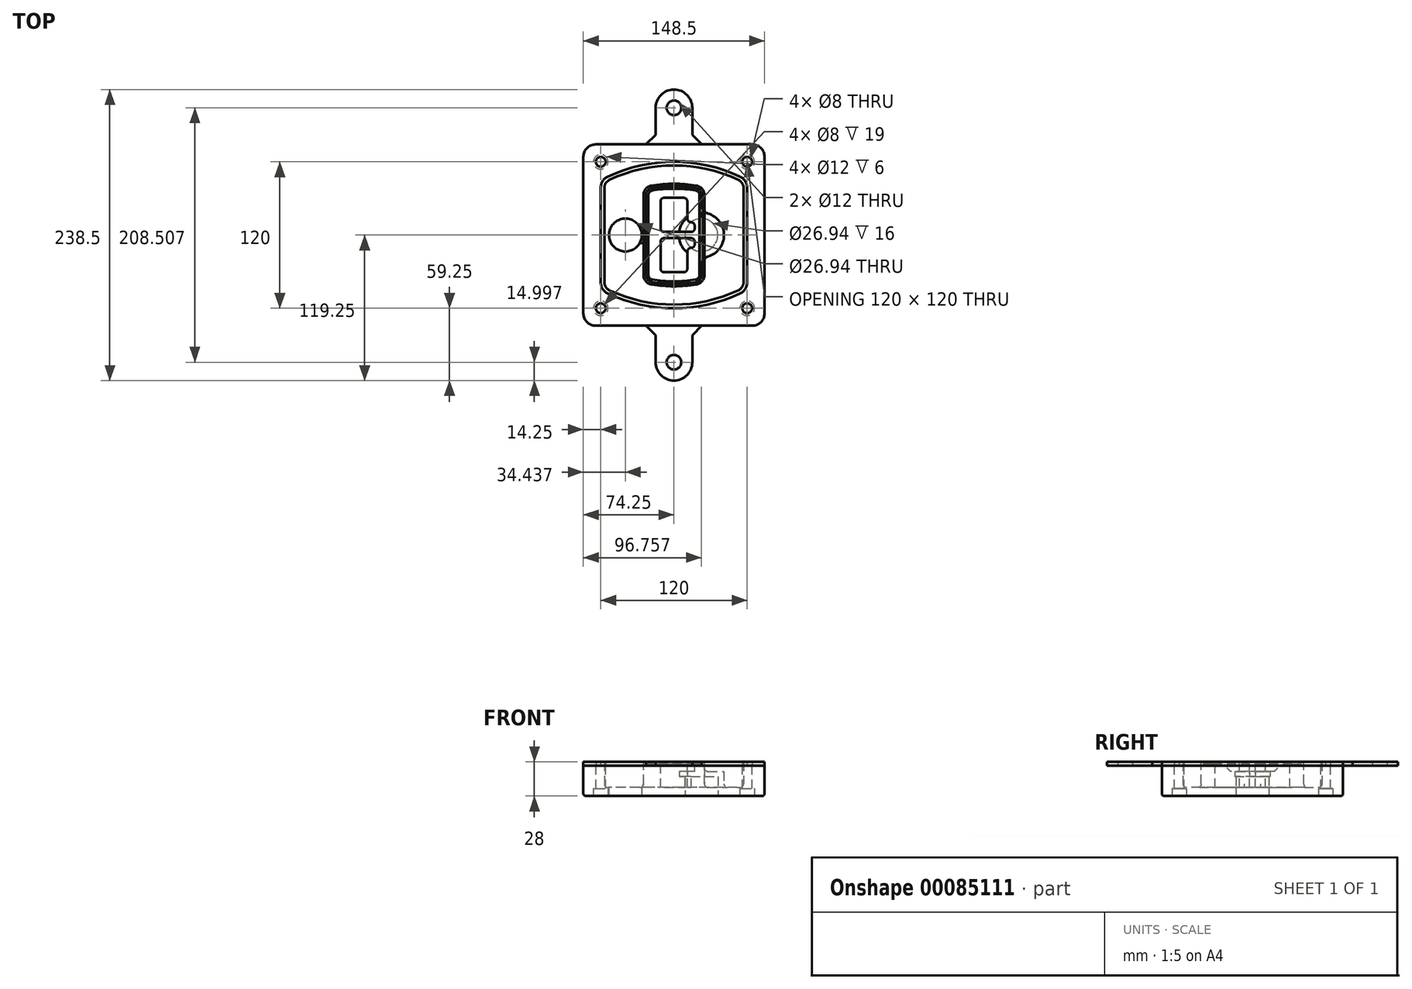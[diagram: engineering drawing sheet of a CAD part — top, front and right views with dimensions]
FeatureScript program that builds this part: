
annotation { "Feature Type Name" : "Feature", "Feature Type Description" : "" }
export const myFeature = defineFeature(function(context is Context, id is Id, definition is map)
    precondition{}
    {
        {
            var Q0;
            Q0=qCreatedBy(makeId("Top.planeOp"),FACE);
            var sketch = newSketch(context, id + "F0", { "sketchPlane" : qUnion([Q0])});
            skPoint(sketch, "E0.rect.middle", {"position": v(0, 0) * mm});
            skLineSegment(sketch, "E1.bottom", {"start": v(-64.25, -74.25) * mm, "end": v(64.25, -74.25) * mm});
            skLineSegment(sketch, "E1.top", {"start": v(-64.25, 74.25) * mm, "end": v(64.25, 74.25) * mm});
            skLineSegment(sketch, "E1.left", {"start": v(-74.25, -64.25) * mm, "end": v(-74.25, 64.25) * mm});
            skLineSegment(sketch, "E1.right", {"start": v(74.25, -64.25) * mm, "end": v(74.25, 64.25) * mm});
            skLineSegment(sketch, "E2", {"start": v(-74.25, 74.25) * mm, "end": v(74.25, -74.25) * mm, "construction": true});
            skLineSegment(sketch, "E3", {"start": v(74.25, 74.25) * mm, "end": v(-74.25, -74.25) * mm, "construction": true});
            skCircle(sketch, "E4", {"center": v(-60, 60) * mm, "radius": 4 * mm});
            skCircle(sketch, "E5", {"center": v(60, 60) * mm, "radius": 4 * mm});
            skCircle(sketch, "E6", {"center": v(60, -60) * mm, "radius": 4 * mm});
            skCircle(sketch, "E7", {"center": v(-60, -60) * mm, "radius": 4 * mm});
            skLineSegment(sketch, "E8", {"start": v(-60, 60) * mm, "end": v(60, 60) * mm, "construction": true});
            skLineSegment(sketch, "E9", {"start": v(60, 60) * mm, "end": v(60, -60) * mm, "construction": true});
            skLineSegment(sketch, "E10", {"start": v(60, -60) * mm, "end": v(-60, -60) * mm, "construction": true});
            skLineSegment(sketch, "E11", {"start": v(-60, -60) * mm, "end": v(-60, 60) * mm, "construction": true});
            skLineSegment(sketch, "E12", {"start": v(-60, 38.83) * mm, "end": v(-60, -38.83) * mm});
            skLineSegment(sketch, "E13", {"start": v(60, 38.83) * mm, "end": v(60, -38.83) * mm});
            skArc(sketch, "E14", {"start": v(54.26, 47.88) * mm, "mid": v(0, 60) * mm, "end": v(-54.26, 47.88) * mm});
            skArc(sketch, "E15", {"start": v(-54.26, -47.88) * mm, "mid": v(0, -60) * mm, "end": v(54.26, -47.88) * mm});
            skLineSegment(sketch, "E16", {"start": v(-60, 0) * mm, "end": v(60, 0) * mm, "construction": true});
            skPoint(sketch, "E17.visualSharp", {"position": v(-60, -45) * mm});
            skArc(sketch, "E17.filletArc", {"start": v(-60, -38.83) * mm, "mid": v(-58.44, -44.2) * mm, "end": v(-54.26, -47.88) * mm});
            skPoint(sketch, "E18.visualSharp", {"position": v(-60, 45) * mm});
            skArc(sketch, "E18.filletArc", {"start": v(-54.26, 47.88) * mm, "mid": v(-58.44, 44.2) * mm, "end": v(-60, 38.83) * mm});
            skPoint(sketch, "E19.visualSharp", {"position": v(60, 45) * mm});
            skArc(sketch, "E19.filletArc", {"start": v(60, 38.83) * mm, "mid": v(58.44, 44.2) * mm, "end": v(54.26, 47.88) * mm});
            skPoint(sketch, "E20.visualSharp", {"position": v(60, -45) * mm});
            skArc(sketch, "E20.filletArc", {"start": v(54.26, -47.88) * mm, "mid": v(58.44, -44.2) * mm, "end": v(60, -38.83) * mm});
            skPoint(sketch, "E21.visualSharp", {"position": v(-74.25, 74.25) * mm});
            skArc(sketch, "E21.filletArc", {"start": v(-64.25, 74.25) * mm, "mid": v(-71.32, 71.32) * mm, "end": v(-74.25, 64.25) * mm});
            skPoint(sketch, "E22.visualSharp", {"position": v(74.25, 74.25) * mm});
            skArc(sketch, "E22.filletArc", {"start": v(74.25, 64.25) * mm, "mid": v(71.32, 71.32) * mm, "end": v(64.25, 74.25) * mm});
            skPoint(sketch, "E23.visualSharp", {"position": v(74.25, -74.25) * mm});
            skArc(sketch, "E23.filletArc", {"start": v(64.25, -74.25) * mm, "mid": v(71.32, -71.32) * mm, "end": v(74.25, -64.25) * mm});
            skPoint(sketch, "E24.visualSharp", {"position": v(-74.25, -74.25) * mm});
            skArc(sketch, "E24.filletArc", {"start": v(-74.25, -64.25) * mm, "mid": v(-71.32, -71.32) * mm, "end": v(-64.25, -74.25) * mm});
            skArc(sketch, "E25.0", {"start": v(57, 38.83) * mm, "mid": v(55.9, 42.58) * mm, "end": v(52.98, 45.17) * mm});
            skLineSegment(sketch, "E25.1", {"start": v(57, 38.83) * mm, "end": v(57, -38.83) * mm});
            skArc(sketch, "E25.2", {"start": v(52.98, -45.17) * mm, "mid": v(55.9, -42.58) * mm, "end": v(57, -38.83) * mm});
            skArc(sketch, "E25.3", {"start": v(-52.98, -45.17) * mm, "mid": v(0, -57) * mm, "end": v(52.98, -45.17) * mm});
            skArc(sketch, "E25.4", {"start": v(-57, -38.83) * mm, "mid": v(-55.9, -42.58) * mm, "end": v(-52.98, -45.17) * mm});
            skArc(sketch, "E25.5", {"start": v(52.98, 45.17) * mm, "mid": v(0, 57) * mm, "end": v(-52.98, 45.17) * mm});
            skLineSegment(sketch, "E25.6", {"start": v(-57, 38.83) * mm, "end": v(-57, -38.83) * mm});
            skArc(sketch, "E25.7", {"start": v(-52.98, 45.17) * mm, "mid": v(-55.9, 42.58) * mm, "end": v(-57, 38.83) * mm});
            skArc(sketch, "E26.0", {"start": v(-55.96, 51.5) * mm, "mid": v(-61.82, 46.33) * mm, "end": v(-64, 38.83) * mm});
            skArc(sketch, "E26.1", {"start": v(55.96, 51.5) * mm, "mid": v(0, 64) * mm, "end": v(-55.96, 51.5) * mm});
            skArc(sketch, "E26.2", {"start": v(64, 38.83) * mm, "mid": v(61.82, 46.33) * mm, "end": v(55.96, 51.5) * mm});
            skLineSegment(sketch, "E26.3", {"start": v(64, 38.83) * mm, "end": v(64, -38.83) * mm});
            skArc(sketch, "E26.4", {"start": v(55.96, -51.5) * mm, "mid": v(61.82, -46.33) * mm, "end": v(64, -38.83) * mm});
            skLineSegment(sketch, "E26.5", {"start": v(-64, 38.83) * mm, "end": v(-64, -38.83) * mm});
            skArc(sketch, "E26.6", {"start": v(-55.96, -51.5) * mm, "mid": v(0, -64) * mm, "end": v(55.96, -51.5) * mm});
            skArc(sketch, "E26.7", {"start": v(-64, -38.83) * mm, "mid": v(-61.82, -46.33) * mm, "end": v(-55.96, -51.5) * mm});
            skSolve(sketch);
        }
        {
            var Q0;
            Q0=makeQuery(id+"F0.imprint","IMPRINT",FACE,{"disambiguationData":[TD([[makeQuery(id+"F0.imprint","IMPRINT",EDGE,{"derivedFrom":sQuery(id+"F0.wireOp",EDGE,"E1.bottom")}),1.0]])]});
            var Q1;
            Q1=makeQuery(id+"F0.imprint","IMPRINT",FACE,{"disambiguationData":[TD([[makeQuery(id+"F0.imprint","IMPRINT",EDGE,{"derivedFrom":sQuery(id+"F0.wireOp",EDGE,"E12")}),1.0]])]});
            var Q2;
            Q2=makeQuery(id+"F0.imprint","IMPRINT",FACE,{"disambiguationData":[TD([[makeQuery(id+"F0.imprint","IMPRINT",EDGE,{"derivedFrom":sQuery(id+"F0.wireOp",EDGE,"E25.0")}),1.0]])]});
            var Q3;
            Q3=makeQuery(id+"F0.imprint","IMPRINT",FACE,{"disambiguationData":[TD([[makeQuery(id+"F0.imprint","IMPRINT",EDGE,{"derivedFrom":sQuery(id+"F0.wireOp",EDGE,"E12")}),-1.0]])]});
            extrude(context, id + "F1", {"entities" : qUnion([Q0, Q1, Q2, Q3]), "oppositeDirection" : true, "depth" : 25 * mm});
        }
        {
            var Q0;
            Q0=makeQuery(id+"F0.imprint","IMPRINT",FACE,{"disambiguationData":[TD([[makeQuery(id+"F0.imprint","IMPRINT",EDGE,{"derivedFrom":sQuery(id+"F0.wireOp",EDGE,"E12")}),1.0]])]});
            extrude(context, id + "F2", {"entities" : qUnion([Q0]), "operationType" : NewBodyOperationType.ADD, "depth" : 3 * mm});
        }
        {
            var Q0;
            Q0=makeQuery(id+"F0.imprint","IMPRINT",FACE,{"disambiguationData":[TD([[makeQuery(id+"F0.imprint","IMPRINT",EDGE,{"derivedFrom":sQuery(id+"F0.wireOp",EDGE,"E25.0")}),1.0]])]});
            extrude(context, id + "F3", {"entities" : qUnion([Q0]), "operationType" : NewBodyOperationType.REMOVE, "oppositeDirection" : true, "depth" : 18 * mm});
        }
        {
            var Q0;
            Q0=makeQuery(id+"F2.opExtrude","CAP_FACE",FACE,{"disambiguationData":[OSD([sQuery(id+"F0.wireOp",EDGE,"E12"),sQuery(id+"F0.wireOp",EDGE,"E13"),sQuery(id+"F0.wireOp",EDGE,"E14"),sQuery(id+"F0.wireOp",EDGE,"E15"),sQuery(id+"F0.wireOp",EDGE,"E17.filletArc"),sQuery(id+"F0.wireOp",EDGE,"E18.filletArc"),sQuery(id+"F0.wireOp",EDGE,"E19.filletArc"),sQuery(id+"F0.wireOp",EDGE,"E20.filletArc"),sQuery(id+"F0.wireOp",EDGE,"E25.0"),sQuery(id+"F0.wireOp",EDGE,"E25.1"),sQuery(id+"F0.wireOp",EDGE,"E25.2"),sQuery(id+"F0.wireOp",EDGE,"E25.3"),sQuery(id+"F0.wireOp",EDGE,"E25.4"),sQuery(id+"F0.wireOp",EDGE,"E25.5"),sQuery(id+"F0.wireOp",EDGE,"E25.6"),sQuery(id+"F0.wireOp",EDGE,"E25.7")])],"isStart":false});
            var sketch = newSketch(context, id + "F4", { "sketchPlane" : qUnion([Q0])});
            skArc(sketch, "E27.0", {"start": v(-18.34, -40.45) * mm, "mid": v(0, -42) * mm, "end": v(18.34, -40.45) * mm});
            skArc(sketch, "E28.0", {"start": v(18.34, 40.45) * mm, "mid": v(0, 42) * mm, "end": v(-18.34, 40.45) * mm});
            skLineSegment(sketch, "E29", {"start": v(-25, 32.57) * mm, "end": v(-25, -32.57) * mm});
            skLineSegment(sketch, "E30", {"start": v(25, 32.57) * mm, "end": v(25, -32.57) * mm});
            skLineSegment(sketch, "E31", {"start": v(-25, 39.1) * mm, "end": v(25, 39.1) * mm, "construction": true});
            skLineSegment(sketch, "E32", {"start": v(-25, -39.1) * mm, "end": v(25, -39.1) * mm, "construction": true});
            skPoint(sketch, "E33.visualSharp", {"position": v(-25, 39.1) * mm});
            skArc(sketch, "E33.filletArc", {"start": v(-18.34, 40.45) * mm, "mid": v(-23.11, 37.73) * mm, "end": v(-25, 32.57) * mm});
            skPoint(sketch, "E34.visualSharp", {"position": v(25, 39.1) * mm});
            skArc(sketch, "E34.filletArc", {"start": v(25, 32.57) * mm, "mid": v(23.11, 37.73) * mm, "end": v(18.34, 40.45) * mm});
            skPoint(sketch, "E35.visualSharp", {"position": v(25, -39.1) * mm});
            skArc(sketch, "E35.filletArc", {"start": v(18.34, -40.45) * mm, "mid": v(23.11, -37.73) * mm, "end": v(25, -32.57) * mm});
            skPoint(sketch, "E36.visualSharp", {"position": v(-25, -39.1) * mm});
            skArc(sketch, "E36.filletArc", {"start": v(-25, -32.57) * mm, "mid": v(-23.11, -37.73) * mm, "end": v(-18.34, -40.45) * mm});
            skArc(sketch, "E37.0", {"start": v(52.98, 45.17) * mm, "mid": v(0, 57) * mm, "end": v(-52.98, 45.17) * mm});
            skArc(sketch, "E37.1", {"start": v(-52.98, 45.17) * mm, "mid": v(-55.9, 42.58) * mm, "end": v(-57, 38.83) * mm});
            skLineSegment(sketch, "E37.2", {"start": v(-57, 38.83) * mm, "end": v(-57, -38.83) * mm});
            skArc(sketch, "E37.3", {"start": v(-57, -38.83) * mm, "mid": v(-55.9, -42.58) * mm, "end": v(-52.98, -45.17) * mm});
            skArc(sketch, "E37.4", {"start": v(-52.98, -45.17) * mm, "mid": v(0, -57) * mm, "end": v(52.98, -45.17) * mm});
            skArc(sketch, "E37.5", {"start": v(52.98, -45.17) * mm, "mid": v(55.9, -42.58) * mm, "end": v(57, -38.83) * mm});
            skLineSegment(sketch, "E37.6", {"start": v(57, 38.83) * mm, "end": v(57, -38.83) * mm});
            skArc(sketch, "E37.7", {"start": v(57, 38.83) * mm, "mid": v(55.9, 42.58) * mm, "end": v(52.98, 45.17) * mm});
            skLineSegment(sketch, "E38.0", {"start": v(23, 32.57) * mm, "end": v(23, -32.57) * mm});
            skArc(sketch, "E38.1", {"start": v(18, -38.48) * mm, "mid": v(21.58, -36.44) * mm, "end": v(23, -32.57) * mm});
            skArc(sketch, "E38.2", {"start": v(-18, -38.48) * mm, "mid": v(0, -40) * mm, "end": v(18, -38.48) * mm});
            skArc(sketch, "E38.3", {"start": v(-23, -32.57) * mm, "mid": v(-21.58, -36.44) * mm, "end": v(-18, -38.48) * mm});
            skLineSegment(sketch, "E38.4", {"start": v(-23, 32.57) * mm, "end": v(-23, -32.57) * mm});
            skArc(sketch, "E38.5", {"start": v(23, 32.57) * mm, "mid": v(21.58, 36.44) * mm, "end": v(18, 38.48) * mm});
            skArc(sketch, "E38.6", {"start": v(-18, 38.48) * mm, "mid": v(-21.58, 36.44) * mm, "end": v(-23, 32.57) * mm});
            skArc(sketch, "E38.7", {"start": v(18, 38.48) * mm, "mid": v(0, 40) * mm, "end": v(-18, 38.48) * mm});
            skArc(sketch, "E39.0", {"start": v(21, 32.57) * mm, "mid": v(20.06, 35.15) * mm, "end": v(17.67, 36.5) * mm});
            skLineSegment(sketch, "E39.1", {"start": v(21, 32.57) * mm, "end": v(21, -32.57) * mm});
            skArc(sketch, "E39.2", {"start": v(17.67, -36.5) * mm, "mid": v(20.06, -35.15) * mm, "end": v(21, -32.57) * mm});
            skArc(sketch, "E39.3", {"start": v(-17.67, -36.5) * mm, "mid": v(0, -38) * mm, "end": v(17.67, -36.5) * mm});
            skArc(sketch, "E39.4", {"start": v(-21, -32.57) * mm, "mid": v(-20.06, -35.15) * mm, "end": v(-17.67, -36.5) * mm});
            skArc(sketch, "E39.5", {"start": v(17.67, 36.5) * mm, "mid": v(0, 38) * mm, "end": v(-17.67, 36.5) * mm});
            skLineSegment(sketch, "E39.6", {"start": v(-21, 32.57) * mm, "end": v(-21, -32.57) * mm});
            skArc(sketch, "E39.7", {"start": v(-17.67, 36.5) * mm, "mid": v(-20.06, 35.15) * mm, "end": v(-21, 32.57) * mm});
            skLineSegment(sketch, "E40", {"start": v(-25, 0) * mm, "end": v(25, 0) * mm, "construction": true});
            skLineSegment(sketch, "E41", {"start": v(-11, 5.5) * mm, "end": v(-11, 27.5) * mm});
            skLineSegment(sketch, "E42", {"start": v(-8, 30.5) * mm, "end": v(8, 30.5) * mm});
            skLineSegment(sketch, "E43", {"start": v(11, 27.5) * mm, "end": v(11, 13.5) * mm});
            skLineSegment(sketch, "E44", {"start": v(14, 10.5) * mm, "end": v(14, 10.5) * mm});
            skLineSegment(sketch, "E45", {"start": v(17, 7.5) * mm, "end": v(17, 5.5) * mm});
            skLineSegment(sketch, "E46", {"start": v(14, 2.5) * mm, "end": v(-8, 2.5) * mm});
            skPoint(sketch, "E47.visualSharp", {"position": v(-11, 30.5) * mm});
            skArc(sketch, "E47.filletArc", {"start": v(-8, 30.5) * mm, "mid": v(-10.12, 29.62) * mm, "end": v(-11, 27.5) * mm});
            skPoint(sketch, "E48.visualSharp", {"position": v(11, 30.5) * mm});
            skArc(sketch, "E48.filletArc", {"start": v(11, 27.5) * mm, "mid": v(10.12, 29.62) * mm, "end": v(8, 30.5) * mm});
            skPoint(sketch, "E49.visualSharp", {"position": v(11, 10.5) * mm});
            skArc(sketch, "E49.filletArc", {"start": v(11, 13.5) * mm, "mid": v(11.88, 11.38) * mm, "end": v(14, 10.5) * mm});
            skPoint(sketch, "E50.visualSharp", {"position": v(17, 10.5) * mm});
            skArc(sketch, "E50.filletArc", {"start": v(17, 7.5) * mm, "mid": v(16.12, 9.62) * mm, "end": v(14, 10.5) * mm});
            skPoint(sketch, "E51.visualSharp", {"position": v(17, 2.5) * mm});
            skArc(sketch, "E51.filletArc", {"start": v(14, 2.5) * mm, "mid": v(16.12, 3.38) * mm, "end": v(17, 5.5) * mm});
            skPoint(sketch, "E52.visualSharp", {"position": v(-11, 2.5) * mm});
            skArc(sketch, "E52.filletArc", {"start": v(-11, 5.5) * mm, "mid": v(-10.12, 3.38) * mm, "end": v(-8, 2.5) * mm});
            skLineSegment(sketch, "E53.0.MirrorCS", {"start": v(14, -2.5) * mm, "end": v(-8, -2.5) * mm});
            skArc(sketch, "E54.0.MirrorCS", {"start": v(-11, -5.5) * mm, "mid": v(-10.12, -3.38) * mm, "end": v(-8, -2.5) * mm});
            skLineSegment(sketch, "E55.0.MirrorCS", {"start": v(-11, -5.5) * mm, "end": v(-11, -27.5) * mm});
            skArc(sketch, "E56.0.MirrorCS", {"start": v(-8, -30.5) * mm, "mid": v(-10.12, -29.62) * mm, "end": v(-11, -27.5) * mm});
            skLineSegment(sketch, "E57.0.MirrorCS", {"start": v(-8, -30.5) * mm, "end": v(8, -30.5) * mm});
            skArc(sketch, "E58.0.MirrorCS", {"start": v(11, -27.5) * mm, "mid": v(10.12, -29.62) * mm, "end": v(8, -30.5) * mm});
            skLineSegment(sketch, "E59.0.MirrorCS", {"start": v(11, -27.5) * mm, "end": v(11, -13.5) * mm});
            skArc(sketch, "E60.0.MirrorCS", {"start": v(11, -13.5) * mm, "mid": v(11.88, -11.38) * mm, "end": v(14, -10.5) * mm});
            skArc(sketch, "E61.0.MirrorCS", {"start": v(17, -7.5) * mm, "mid": v(16.12, -9.62) * mm, "end": v(14, -10.5) * mm});
            skLineSegment(sketch, "E62.0.MirrorCS", {"start": v(17, -7.5) * mm, "end": v(17, -5.5) * mm});
            skArc(sketch, "E63.0.MirrorCS", {"start": v(14, -2.5) * mm, "mid": v(16.12, -3.38) * mm, "end": v(17, -5.5) * mm});
            skSolve(sketch);
        }
        {
            var Q0;
            Q0=makeQuery(id+"F4.imprint","IMPRINT",FACE,{"disambiguationData":[TD([[makeQuery(id+"F4.imprint","IMPRINT",EDGE,{"derivedFrom":sQuery(id+"F4.wireOp",EDGE,"E27.0")}),1.0]])]});
            var Q1;
            Q1=makeQuery(id+"F4.imprint","IMPRINT",FACE,{"disambiguationData":[TD([[makeQuery(id+"F4.imprint","IMPRINT",EDGE,{"derivedFrom":sQuery(id+"F4.wireOp",EDGE,"E38.0")}),-1.0]])]});
            var Q2;
            Q2=makeQuery(id+"F4.imprint","IMPRINT",FACE,{"disambiguationData":[TD([[makeQuery(id+"F4.imprint","IMPRINT",EDGE,{"derivedFrom":sQuery(id+"F4.wireOp",EDGE,"E39.0")}),1.0]])]});
            extrude(context, id + "F5", {"entities" : qUnion([Q0, Q1, Q2]), "operationType" : NewBodyOperationType.ADD, "endBound" : BoundingType.UP_TO_NEXT, "oppositeDirection" : true, "depth" : 25 * mm});
        }
        {
            var Q0;
            Q0=makeQuery(id+"F4.imprint","IMPRINT",FACE,{"disambiguationData":[TD([[makeQuery(id+"F4.imprint","IMPRINT",EDGE,{"derivedFrom":sQuery(id+"F4.wireOp",EDGE,"E38.0")}),-1.0]])]});
            extrude(context, id + "F6", {"entities" : qUnion([Q0]), "operationType" : NewBodyOperationType.REMOVE, "oppositeDirection" : true, "depth" : 2 * mm});
        }
        {
            var Q0;
            Q0=makeQuery(id+"F1.opExtrude","CAP_FACE",FACE,{"disambiguationData":[OSD([sQuery(id+"F0.wireOp",EDGE,"E1.bottom"),sQuery(id+"F0.wireOp",EDGE,"E1.top"),sQuery(id+"F0.wireOp",EDGE,"E1.left"),sQuery(id+"F0.wireOp",EDGE,"E1.right"),sQuery(id+"F0.wireOp",EDGE,"E4"),sQuery(id+"F0.wireOp",EDGE,"E5"),sQuery(id+"F0.wireOp",EDGE,"E6"),sQuery(id+"F0.wireOp",EDGE,"E7"),sQuery(id+"F0.wireOp",EDGE,"E21.filletArc"),sQuery(id+"F0.wireOp",EDGE,"E22.filletArc"),sQuery(id+"F0.wireOp",EDGE,"E23.filletArc"),sQuery(id+"F0.wireOp",EDGE,"E24.filletArc")])],"isStart":false});
            var sketch = newSketch(context, id + "F7", { "sketchPlane" : qUnion([Q0])});
            skCircle(sketch, "E64", {"center": v(22.5, 0) * mm, "radius": 13.47 * mm});
            skCircle(sketch, "E65", {"center": v(-39.81, 0) * mm, "radius": 13.47 * mm});
            skLineSegment(sketch, "E66", {"start": v(74.25, 0) * mm, "end": v(-74.25, 0) * mm});
            skCircle(sketch, "E67", {"center": v(22.5, 0) * mm, "radius": 18.47 * mm});
            skCircle(sketch, "E68", {"center": v(60, -60) * mm, "radius": 6 * mm});
            skCircle(sketch, "E69", {"center": v(-60, -60) * mm, "radius": 6 * mm});
            skCircle(sketch, "E70", {"center": v(-60, 60) * mm, "radius": 6 * mm});
            skCircle(sketch, "E71", {"center": v(60, 60) * mm, "radius": 6 * mm});
            skSolve(sketch);
        }
        {
            var Q0;
            {var subQ1=sQuery(id+"F7.wireOp",EDGE,"E66");var subQ4=sQuery(id+"F7.wireOp",EDGE,"E64");var subQ6=makeQuery(id+"F7.imprint","INTERSECT",VERTEX,{"disambiguationData":[OD(0.0)],"derivedFrom":[subQ4,subQ1]});Q0=makeQuery(id+"F7.imprint","IMPRINT",FACE,{"disambiguationData":[TD([[makeQuery(id+"F7.imprint","IMPRINT",EDGE,{"disambiguationData":[TD([[subQ6,-1.0]])],"derivedFrom":subQ4}),-1.0]])]});}
            var Q1;
            {var subQ0=sQuery(id+"F7.wireOp",EDGE,"E66");var subQ1=sQuery(id+"F7.wireOp",EDGE,"E64");var subQ3=makeQuery(id+"F7.imprint","INTERSECT",VERTEX,{"disambiguationData":[OD(0.0)],"derivedFrom":[subQ1,subQ0]});Q1=makeQuery(id+"F7.imprint","IMPRINT",FACE,{"disambiguationData":[TD([[makeQuery(id+"F7.imprint","IMPRINT",EDGE,{"disambiguationData":[TD([[subQ3,-1.0]])],"derivedFrom":subQ1}),1.0]])]});}
            var Q2;
            {var subQ0=sQuery(id+"F7.wireOp",EDGE,"E66");var subQ1=sQuery(id+"F7.wireOp",EDGE,"E64");var subQ3=makeQuery(id+"F7.imprint","INTERSECT",VERTEX,{"disambiguationData":[OD(0.0)],"derivedFrom":[subQ1,subQ0]});Q2=makeQuery(id+"F7.imprint","IMPRINT",FACE,{"disambiguationData":[TD([[makeQuery(id+"F7.imprint","IMPRINT",EDGE,{"disambiguationData":[TD([[subQ3,1.0]])],"derivedFrom":subQ1}),1.0]])]});}
            var Q3;
            {var subQ1=sQuery(id+"F7.wireOp",EDGE,"E66");var subQ4=sQuery(id+"F7.wireOp",EDGE,"E64");var subQ6=makeQuery(id+"F7.imprint","INTERSECT",VERTEX,{"disambiguationData":[OD(0.0)],"derivedFrom":[subQ4,subQ1]});Q3=makeQuery(id+"F7.imprint","IMPRINT",FACE,{"disambiguationData":[TD([[makeQuery(id+"F7.imprint","IMPRINT",EDGE,{"disambiguationData":[TD([[subQ6,1.0]])],"derivedFrom":subQ4}),-1.0]])]});}
            extrude(context, id + "F8", {"entities" : qUnion([Q0, Q1, Q2, Q3]), "operationType" : NewBodyOperationType.ADD, "oppositeDirection" : true, "depth" : 20 * mm});
        }
        {
            var Q0;
            {var subQ0=sQuery(id+"F7.wireOp",EDGE,"E66");var subQ1=sQuery(id+"F7.wireOp",EDGE,"E64");var subQ3=makeQuery(id+"F7.imprint","INTERSECT",VERTEX,{"disambiguationData":[OD(0.0)],"derivedFrom":[subQ1,subQ0]});Q0=makeQuery(id+"F7.imprint","IMPRINT",FACE,{"disambiguationData":[TD([[makeQuery(id+"F7.imprint","IMPRINT",EDGE,{"disambiguationData":[TD([[subQ3,-1.0]])],"derivedFrom":subQ1}),1.0]])]});}
            var Q1;
            {var subQ0=sQuery(id+"F7.wireOp",EDGE,"E66");var subQ1=sQuery(id+"F7.wireOp",EDGE,"E64");var subQ3=makeQuery(id+"F7.imprint","INTERSECT",VERTEX,{"disambiguationData":[OD(0.0)],"derivedFrom":[subQ1,subQ0]});Q1=makeQuery(id+"F7.imprint","IMPRINT",FACE,{"disambiguationData":[TD([[makeQuery(id+"F7.imprint","IMPRINT",EDGE,{"disambiguationData":[TD([[subQ3,1.0]])],"derivedFrom":subQ1}),1.0]])]});}
            extrude(context, id + "F9", {"entities" : qUnion([Q0, Q1]), "operationType" : NewBodyOperationType.REMOVE, "oppositeDirection" : true, "depth" : 16 * mm});
        }
        {
            var Q0;
            {var subQ0=sQuery(id+"F7.wireOp",EDGE,"E66");var subQ1=sQuery(id+"F7.wireOp",EDGE,"E65");var subQ3=makeQuery(id+"F7.imprint","INTERSECT",VERTEX,{"disambiguationData":[OD(0.0)],"derivedFrom":[subQ1,subQ0]});Q0=makeQuery(id+"F7.imprint","IMPRINT",FACE,{"disambiguationData":[TD([[makeQuery(id+"F7.imprint","IMPRINT",EDGE,{"disambiguationData":[TD([[subQ3,-1.0]])],"derivedFrom":subQ1}),1.0]])]});}
            var Q1;
            {var subQ0=sQuery(id+"F7.wireOp",EDGE,"E66");var subQ1=sQuery(id+"F7.wireOp",EDGE,"E65");var subQ3=makeQuery(id+"F7.imprint","INTERSECT",VERTEX,{"disambiguationData":[OD(0.0)],"derivedFrom":[subQ1,subQ0]});Q1=makeQuery(id+"F7.imprint","IMPRINT",FACE,{"disambiguationData":[TD([[makeQuery(id+"F7.imprint","IMPRINT",EDGE,{"disambiguationData":[TD([[subQ3,1.0]])],"derivedFrom":subQ1}),1.0]])]});}
            extrude(context, id + "F10", {"entities" : qUnion([Q0, Q1]), "operationType" : NewBodyOperationType.REMOVE, "oppositeDirection" : true, "depth" : 25 * mm});
        }
        {
            var Q0;
            Q0=makeQuery(id+"F7.imprint","IMPRINT",FACE,{"disambiguationData":[TD([[makeQuery(id+"F7.imprint","IMPRINT",EDGE,{"derivedFrom":sQuery(id+"F7.wireOp",EDGE,"E68")}),1.0]])]});
            var Q1;
            Q1=makeQuery(id+"F7.imprint","IMPRINT",FACE,{"disambiguationData":[TD([[makeQuery(id+"F7.imprint","IMPRINT",EDGE,{"derivedFrom":makeQuery(id+"F1.opExtrude","CAP_EDGE",EDGE,{"disambiguationData":[OSD([sQuery(id+"F0.wireOp",EDGE,"E5")])],"isStart":false})}),-1.0]])]});
            var Q2;
            Q2=makeQuery(id+"F7.imprint","IMPRINT",FACE,{"disambiguationData":[TD([[makeQuery(id+"F7.imprint","IMPRINT",EDGE,{"derivedFrom":sQuery(id+"F7.wireOp",EDGE,"E69")}),1.0]])]});
            var Q3;
            Q3=makeQuery(id+"F7.imprint","IMPRINT",FACE,{"disambiguationData":[TD([[makeQuery(id+"F7.imprint","IMPRINT",EDGE,{"derivedFrom":makeQuery(id+"F1.opExtrude","CAP_EDGE",EDGE,{"disambiguationData":[OSD([sQuery(id+"F0.wireOp",EDGE,"E4")])],"isStart":false})}),-1.0]])]});
            var Q4;
            Q4=makeQuery(id+"F7.imprint","IMPRINT",FACE,{"disambiguationData":[TD([[makeQuery(id+"F7.imprint","IMPRINT",EDGE,{"derivedFrom":sQuery(id+"F7.wireOp",EDGE,"E70")}),1.0]])]});
            var Q5;
            Q5=makeQuery(id+"F7.imprint","IMPRINT",FACE,{"disambiguationData":[TD([[makeQuery(id+"F7.imprint","IMPRINT",EDGE,{"derivedFrom":makeQuery(id+"F1.opExtrude","CAP_EDGE",EDGE,{"disambiguationData":[OSD([sQuery(id+"F0.wireOp",EDGE,"E7")])],"isStart":false})}),-1.0]])]});
            var Q6;
            Q6=makeQuery(id+"F7.imprint","IMPRINT",FACE,{"disambiguationData":[TD([[makeQuery(id+"F7.imprint","IMPRINT",EDGE,{"derivedFrom":sQuery(id+"F7.wireOp",EDGE,"E71")}),1.0]])]});
            var Q7;
            Q7=makeQuery(id+"F7.imprint","IMPRINT",FACE,{"disambiguationData":[TD([[makeQuery(id+"F7.imprint","IMPRINT",EDGE,{"derivedFrom":makeQuery(id+"F1.opExtrude","CAP_EDGE",EDGE,{"disambiguationData":[OSD([sQuery(id+"F0.wireOp",EDGE,"E6")])],"isStart":false})}),-1.0]])]});
            extrude(context, id + "F11", {"entities" : qUnion([Q0, Q1, Q2, Q3, Q4, Q5, Q6, Q7]), "operationType" : NewBodyOperationType.REMOVE, "oppositeDirection" : true, "depth" : 6 * mm});
        }
        {
            var Q0;
            Q0=makeQuery(id+"F9.boolean.opBoolean","COPY",FACE,{"derivedFrom":makeQuery(id+"F9.opExtrude","CAP_FACE",FACE,{"disambiguationData":[OSD([sQuery(id+"F7.wireOp",EDGE,"E64")])],"isStart":false})});
            var sketch = newSketch(context, id + "F12", { "sketchPlane" : qUnion([Q0])});
            skArc(sketch, "E72.0", {"start": v(11, 14.45) * mm, "mid": v(6.45, 9.13) * mm, "end": v(4.2, 2.5) * mm});
            skArc(sketch, "E72.1", {"start": v(4.2, -2.5) * mm, "mid": v(6.45, -9.13) * mm, "end": v(11, -14.45) * mm});
            skLineSegment(sketch, "E73", {"start": v(4.2, -2.5) * mm, "end": v(14, -2.5) * mm});
            skLineSegment(sketch, "E74.0", {"start": v(14, 2.5) * mm, "end": v(4.2, 2.5) * mm});
            skArc(sketch, "E74.1", {"start": v(14, 2.5) * mm, "mid": v(16.12, 3.38) * mm, "end": v(17, 5.5) * mm});
            skLineSegment(sketch, "E74.2", {"start": v(17, 7.5) * mm, "end": v(17, 5.5) * mm});
            skArc(sketch, "E74.3", {"start": v(17, 7.5) * mm, "mid": v(16.12, 9.62) * mm, "end": v(14, 10.5) * mm});
            skArc(sketch, "E74.4", {"start": v(11, 13.5) * mm, "mid": v(11.88, 11.38) * mm, "end": v(14, 10.5) * mm});
            skLineSegment(sketch, "E74.5", {"start": v(11, 14.45) * mm, "end": v(11, 13.5) * mm});
            skLineSegment(sketch, "E74.7", {"start": v(14, -2.5) * mm, "end": v(4.2, -2.5) * mm});
            skArc(sketch, "E74.8", {"start": v(14, -2.5) * mm, "mid": v(16.12, -3.38) * mm, "end": v(17, -5.5) * mm});
            skLineSegment(sketch, "E74.9", {"start": v(17, -7.5) * mm, "end": v(17, -5.5) * mm});
            skArc(sketch, "E74.10", {"start": v(17, -7.5) * mm, "mid": v(16.12, -9.62) * mm, "end": v(14, -10.5) * mm});
            skArc(sketch, "E74.11", {"start": v(11, -13.5) * mm, "mid": v(11.88, -11.38) * mm, "end": v(14, -10.5) * mm});
            skLineSegment(sketch, "E74.12", {"start": v(11, -14.45) * mm, "end": v(11, -13.5) * mm});
            skPoint(sketch, "E75.orphan", {"position": v(11, -27.5) * mm});
            skPoint(sketch, "E76.orphan", {"position": v(-8, -2.5) * mm});
            skPoint(sketch, "E77.orphan", {"position": v(-8, 2.5) * mm});
            skPoint(sketch, "E78.orphan", {"position": v(11, 27.5) * mm});
            skSolve(sketch);
        }
        {
            var Q0;
            {var subQ7=sQuery(id+"F12.wireOp",EDGE,"E72.0");var subQ14=sQuery(id+"F12.wireOp",EDGE,"E72.1");var subQ16=sQuery(id+"F12.wireOp",EDGE,"E74.1");var subQ18=sQuery(id+"F12.wireOp",EDGE,"E74.8");Q0=qUnion([makeQuery(id+"F12.imprint","IMPRINT",FACE,{"disambiguationData":[TD([[makeQuery(id+"F12.imprint","IMPRINT",EDGE,{"derivedFrom":subQ7}),1.0]])]}),makeQuery(id+"F12.imprint","IMPRINT",FACE,{"disambiguationData":[TD([[makeQuery(id+"F12.imprint","IMPRINT",EDGE,{"derivedFrom":subQ14}),1.0]])]}),makeQuery(id+"F12.imprint","IMPRINT",FACE,{"disambiguationData":[TD([[makeQuery(id+"F12.imprint","IMPRINT",EDGE,{"derivedFrom":subQ16}),1.0]])]}),makeQuery(id+"F12.imprint","IMPRINT",FACE,{"disambiguationData":[TD([[makeQuery(id+"F12.imprint","IMPRINT",EDGE,{"derivedFrom":subQ18}),-1.0]])]})]);}
            var Q1;
            Q1=makeQuery(id+"F5.boolean.opBoolean","SPLIT",FACE,{"disambiguationData":[TD([makeQuery(id+"F5.opExtrude","SWEPT_FACE",FACE,{"disambiguationData":[OSD([sQuery(id+"F4.wireOp",EDGE,"E41")])]})])],"derivedFrom":makeQuery(id+"F3.boolean.opBoolean","COPY",FACE,{"derivedFrom":makeQuery(id+"F3.opExtrude","CAP_FACE",FACE,{"disambiguationData":[OSD([sQuery(id+"F0.wireOp",EDGE,"E25.0"),sQuery(id+"F0.wireOp",EDGE,"E25.1"),sQuery(id+"F0.wireOp",EDGE,"E25.2"),sQuery(id+"F0.wireOp",EDGE,"E25.3"),sQuery(id+"F0.wireOp",EDGE,"E25.4"),sQuery(id+"F0.wireOp",EDGE,"E25.5"),sQuery(id+"F0.wireOp",EDGE,"E25.6"),sQuery(id+"F0.wireOp",EDGE,"E25.7")])],"isStart":false})})});
            extrude(context, id + "F13", {"entities" : qUnion([Q0]), "operationType" : NewBodyOperationType.REMOVE, "endBound" : BoundingType.UP_TO_SURFACE, "endBoundEntityFace" : qUnion([Q1]), "depth" : 25 * mm});
        }
        {
            var Q0;
            Q0=makeQuery(id+"F3.boolean.opBoolean","COPY",EDGE,{"derivedFrom":makeQuery(id+"F3.opExtrude","CAP_EDGE",EDGE,{"disambiguationData":[OSD([sQuery(id+"F0.wireOp",EDGE,"E25.6")])],"isStart":false})});
            var Q1;
            Q1=makeQuery(id+"F8.boolean.opBoolean","INTERSECT",EDGE,{"derivedFrom":[makeQuery(id+"F5.opExtrude","SWEPT_FACE",FACE,{"disambiguationData":[OSD([sQuery(id+"F4.wireOp",EDGE,"E30")])]}),makeQuery(id+"F8.opExtrude","CAP_FACE",FACE,{"disambiguationData":[OSD([sQuery(id+"F7.wireOp",EDGE,"E67")])],"isStart":false})]});
            var Q2;
            Q2=makeQuery(id+"F8.boolean.opBoolean","INTERSECT",EDGE,{"disambiguationData":[OD(1.0)],"derivedFrom":[makeQuery(id+"F5.opExtrude","SWEPT_FACE",FACE,{"disambiguationData":[OSD([sQuery(id+"F4.wireOp",EDGE,"E30")])]}),makeQuery(id+"F8.opExtrude","SWEPT_FACE",FACE,{"disambiguationData":[OSD([sQuery(id+"F7.wireOp",EDGE,"E67")])]})]});
            var Q3;
            {var subQ0=sQuery(id+"F4.wireOp",EDGE,"E30");Q3=makeQuery(id+"F8.boolean.opBoolean","SPLIT",EDGE,{"disambiguationData":[TD([makeQuery(id+"F5.opExtrude","SWEPT_FACE",FACE,{"disambiguationData":[OSD([sQuery(id+"F4.wireOp",EDGE,"E35.filletArc")])]})])],"derivedFrom":makeQuery(id+"F5.opExtrude","CAP_EDGE",EDGE,{"disambiguationData":[OSD([subQ0])],"isStart":false})});}
            var Q4;
            {var subQ0=sQuery(id+"F0.wireOp",EDGE,"E25.7");var subQ1=sQuery(id+"F0.wireOp",EDGE,"E25.1");var subQ2=sQuery(id+"F0.wireOp",EDGE,"E25.6");var subQ3=sQuery(id+"F0.wireOp",EDGE,"E25.5");var subQ4=sQuery(id+"F0.wireOp",EDGE,"E25.4");var subQ5=sQuery(id+"F0.wireOp",EDGE,"E25.0");var subQ6=sQuery(id+"F0.wireOp",EDGE,"E25.2");var subQ7=sQuery(id+"F0.wireOp",EDGE,"E25.3");Q4=makeQuery(id+"F8.boolean.opBoolean","INTERSECT",EDGE,{"derivedFrom":[makeQuery(id+"F5.boolean.opBoolean","SPLIT",FACE,{"disambiguationData":[TD([makeQuery(id+"F2.opExtrude","SWEPT_FACE",FACE,{"disambiguationData":[OSD([subQ5])]})])],"derivedFrom":makeQuery(id+"F3.boolean.opBoolean","COPY",FACE,{"derivedFrom":makeQuery(id+"F3.opExtrude","CAP_FACE",FACE,{"disambiguationData":[OSD([subQ5,subQ1,subQ6,subQ7,subQ4,subQ3,subQ2,subQ0])],"isStart":false})})}),makeQuery(id+"F8.opExtrude","SWEPT_FACE",FACE,{"disambiguationData":[OSD([sQuery(id+"F7.wireOp",EDGE,"E67")])]})]});}
            var Q5;
            Q5=makeQuery(id+"F8.boolean.opBoolean","INTERSECT",EDGE,{"disambiguationData":[OD(0.0)],"derivedFrom":[makeQuery(id+"F5.opExtrude","SWEPT_FACE",FACE,{"disambiguationData":[OSD([sQuery(id+"F4.wireOp",EDGE,"E30")])]}),makeQuery(id+"F8.opExtrude","SWEPT_FACE",FACE,{"disambiguationData":[OSD([sQuery(id+"F7.wireOp",EDGE,"E67")])]})]});
            fillet(context, id + "F14", {"entities" : qUnion([Q0, Q1, Q2, Q3, Q4, Q5]), "radius" : 3 * mm, "tangentPropagation" : true, "allowEdgeOverflow" : false});
        }
        {
            var Q0;
            Q0=makeQuery(id+"F1.opExtrude","CAP_EDGE",EDGE,{"disambiguationData":[OSD([sQuery(id+"F0.wireOp",EDGE,"E1.bottom")])],"isStart":false});
            fillet(context, id + "F15", {"entities" : qUnion([Q0]), "radius" : 2 * mm, "tangentPropagation" : true, "allowEdgeOverflow" : false});
        }
        {
            var Q0;
            Q0=qCreatedBy(makeId("Top.planeOp"),FACE);
            var sketch = newSketch(context, id + "F16", { "sketchPlane" : qUnion([Q0])});
            skLineSegment(sketch, "E79", {"start": v(0, 74.25) * mm, "end": v(0, 104.25) * mm, "construction": true});
            skCircle(sketch, "E80", {"center": v(0, 104.25) * mm, "radius": 6 * mm});
            skArc(sketch, "E81", {"start": v(15, 104.25) * mm, "mid": v(0, 119.25) * mm, "end": v(-15, 104.25) * mm});
            skLineSegment(sketch, "E82", {"start": v(15, 104.25) * mm, "end": v(15, 82.1) * mm});
            skLineSegment(sketch, "E83", {"start": v(-15, 104.25) * mm, "end": v(-15, 82.1) * mm});
            skLineSegment(sketch, "E84", {"start": v(15, 82.1) * mm, "end": v(22.84, 74.25) * mm});
            skLineSegment(sketch, "E85", {"start": v(-15, 82.1) * mm, "end": v(-22.84, 74.25) * mm});
            skLineSegment(sketch, "E86", {"start": v(-22.84, 74.25) * mm, "end": v(22.84, 74.25) * mm});
            skLineSegment(sketch, "E87", {"start": v(-15, 104.25) * mm, "end": v(69.43, 104.25) * mm, "construction": true});
            skLineSegment(sketch, "E88", {"start": v(-70.97, 0) * mm, "end": v(73.4, 0) * mm, "construction": true});
            skArc(sketch, "E89.MirrorCS", {"start": v(15, -104.25) * mm, "mid": v(0, -119.25) * mm, "end": v(-15, -104.25) * mm});
            skCircle(sketch, "E90.MirrorC", {"center": v(0, -104.25) * mm, "radius": 6 * mm});
            skLineSegment(sketch, "E91.MirrorCS", {"start": v(15, -104.25) * mm, "end": v(15, -82.1) * mm});
            skLineSegment(sketch, "E92.MirrorCS", {"start": v(-15, -104.25) * mm, "end": v(-15, -82.1) * mm});
            skLineSegment(sketch, "E93.MirrorCS", {"start": v(0, -74.25) * mm, "end": v(0, -104.25) * mm, "construction": true});
            skLineSegment(sketch, "E94.MirrorCS", {"start": v(-15, -82.1) * mm, "end": v(-22.84, -74.25) * mm});
            skLineSegment(sketch, "E95.MirrorCS", {"start": v(15, -82.1) * mm, "end": v(22.84, -74.25) * mm});
            skLineSegment(sketch, "E96.MirrorCS", {"start": v(-22.84, -74.25) * mm, "end": v(22.84, -74.25) * mm});
            skLineSegment(sketch, "E97.MirrorCS", {"start": v(-15, -104.25) * mm, "end": v(69.43, -104.25) * mm, "construction": true});
            skSolve(sketch);
        }
        {
            var Q0;
            Q0 = qSketchRegion(id + "F16", true);
            var Q1;
            {var subQ0=sQuery(id+"F0.wireOp",EDGE,"E22.filletArc");var subQ1=sQuery(id+"F0.wireOp",EDGE,"E7");var subQ2=sQuery(id+"F0.wireOp",EDGE,"E6");var subQ3=sQuery(id+"F0.wireOp",EDGE,"E5");var subQ4=sQuery(id+"F0.wireOp",EDGE,"E4");var subQ5=sQuery(id+"F0.wireOp",EDGE,"E1.bottom");var subQ6=sQuery(id+"F0.wireOp",EDGE,"E21.filletArc");var subQ7=sQuery(id+"F0.wireOp",EDGE,"E1.top");var subQ8=sQuery(id+"F0.wireOp",EDGE,"E1.left");var subQ9=sQuery(id+"F0.wireOp",EDGE,"E1.right");var subQ10=sQuery(id+"F0.wireOp",EDGE,"E23.filletArc");var subQ11=sQuery(id+"F0.wireOp",EDGE,"E24.filletArc");Q1=makeQuery(id+"F2.boolean.opBoolean","SPLIT",FACE,{"disambiguationData":[TD([makeQuery(id+"F1.opExtrude","SWEPT_FACE",FACE,{"disambiguationData":[OSD([subQ5])]})])],"derivedFrom":makeQuery(id+"F1.opExtrude","CAP_FACE",FACE,{"disambiguationData":[OSD([subQ5,subQ7,subQ8,subQ9,subQ4,subQ3,subQ2,subQ1,subQ6,subQ0,subQ10,subQ11])],"isStart":true})});}
            var Q2;
            Q2=makeQuery(id+"F2.opExtrude","CAP_FACE",FACE,{"disambiguationData":[OSD([sQuery(id+"F0.wireOp",EDGE,"E12"),sQuery(id+"F0.wireOp",EDGE,"E13"),sQuery(id+"F0.wireOp",EDGE,"E14"),sQuery(id+"F0.wireOp",EDGE,"E15"),sQuery(id+"F0.wireOp",EDGE,"E17.filletArc"),sQuery(id+"F0.wireOp",EDGE,"E18.filletArc"),sQuery(id+"F0.wireOp",EDGE,"E19.filletArc"),sQuery(id+"F0.wireOp",EDGE,"E20.filletArc"),sQuery(id+"F0.wireOp",EDGE,"E25.0"),sQuery(id+"F0.wireOp",EDGE,"E25.1"),sQuery(id+"F0.wireOp",EDGE,"E25.2"),sQuery(id+"F0.wireOp",EDGE,"E25.3"),sQuery(id+"F0.wireOp",EDGE,"E25.4"),sQuery(id+"F0.wireOp",EDGE,"E25.5"),sQuery(id+"F0.wireOp",EDGE,"E25.6"),sQuery(id+"F0.wireOp",EDGE,"E25.7")])],"isStart":false});
            extrude(context, id + "F17", {"entities" : qUnion([Q0, Q1]), "endBound" : BoundingType.UP_TO_SURFACE, "endBoundEntityFace" : qUnion([Q2]), "depth" : 25 * mm});
        }
    });
